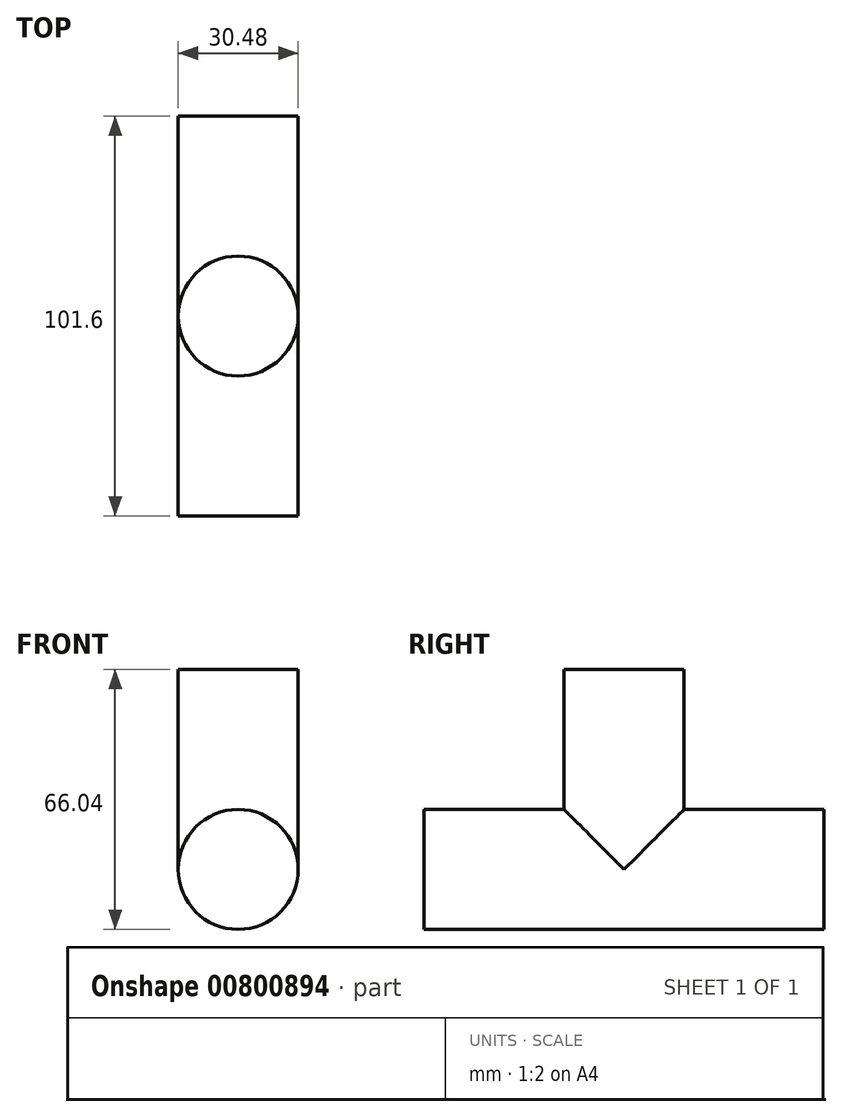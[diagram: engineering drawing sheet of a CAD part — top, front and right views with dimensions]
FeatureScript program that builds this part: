
annotation { "Feature Type Name" : "Feature", "Feature Type Description" : "" }
export const myFeature = defineFeature(function(context is Context, id is Id, definition is map)
    precondition{}
    {
        {
            var Q0;
            Q0=qCreatedBy(makeId("Right.planeOp"),FACE);
            var sketch = newSketch(context, id + "F0", { "sketchPlane" : qUnion([Q0])});
            skLineSegment(sketch, "E0", {"start": v(0, 0) * mm, "end": v(50.8, 0) * mm});
            skLineSegment(sketch, "E1", {"start": v(0, 0) * mm, "end": v(-50.8, 0) * mm});
            skLineSegment(sketch, "E2", {"start": v(0, 0) * mm, "end": v(0, 50.8) * mm});
            skSolve(sketch);
        }
        {
            var Q0;
            Q0=qCreatedBy(makeId("Front.planeOp"),FACE);
            var sketch = newSketch(context, id + "F1", { "sketchPlane" : qUnion([Q0])});
            skCircle(sketch, "E3", {"center": v(0, 0) * mm, "radius": 15.24 * mm});
            skSolve(sketch);
        }
        {
            var Q0;
            Q0=makeQuery(id+"F1.imprint","IMPRINT",FACE,{"disambiguationData":[TD([[makeQuery(id+"F1.imprint","IMPRINT",EDGE,{"derivedFrom":sQuery(id+"F1.wireOp",EDGE,"E3")}),1.0]])]});
            var Q1;
            Q1=sQuery(id+"F0.wireOp",EDGE,"E1");
            var Q2;
            Q2=sQuery(id+"F0.wireOp",EDGE,"E0");
            sweep(context, id + "F2", {"profiles" : qUnion([Q0]), "path" : qUnion([Q1, Q2])});
        }
        {
            var Q0;
            Q0=qCreatedBy(makeId("Top.planeOp"),FACE);
            var sketch = newSketch(context, id + "F3", { "sketchPlane" : qUnion([Q0])});
            skCircle(sketch, "E4", {"center": v(0, 0) * mm, "radius": 15.24 * mm});
            skSolve(sketch);
        }
        {
            var Q0;
            Q0=qSketchRegion(id+"F3",true);
            var Q1;
            Q1=sQuery(id+"F0.wireOp",EDGE,"E2");
            sweep(context, id + "F4", {"operationType" : NewBodyOperationType.ADD, "profiles" : qUnion([Q0]), "path" : qUnion([Q1])});
        }
    });
